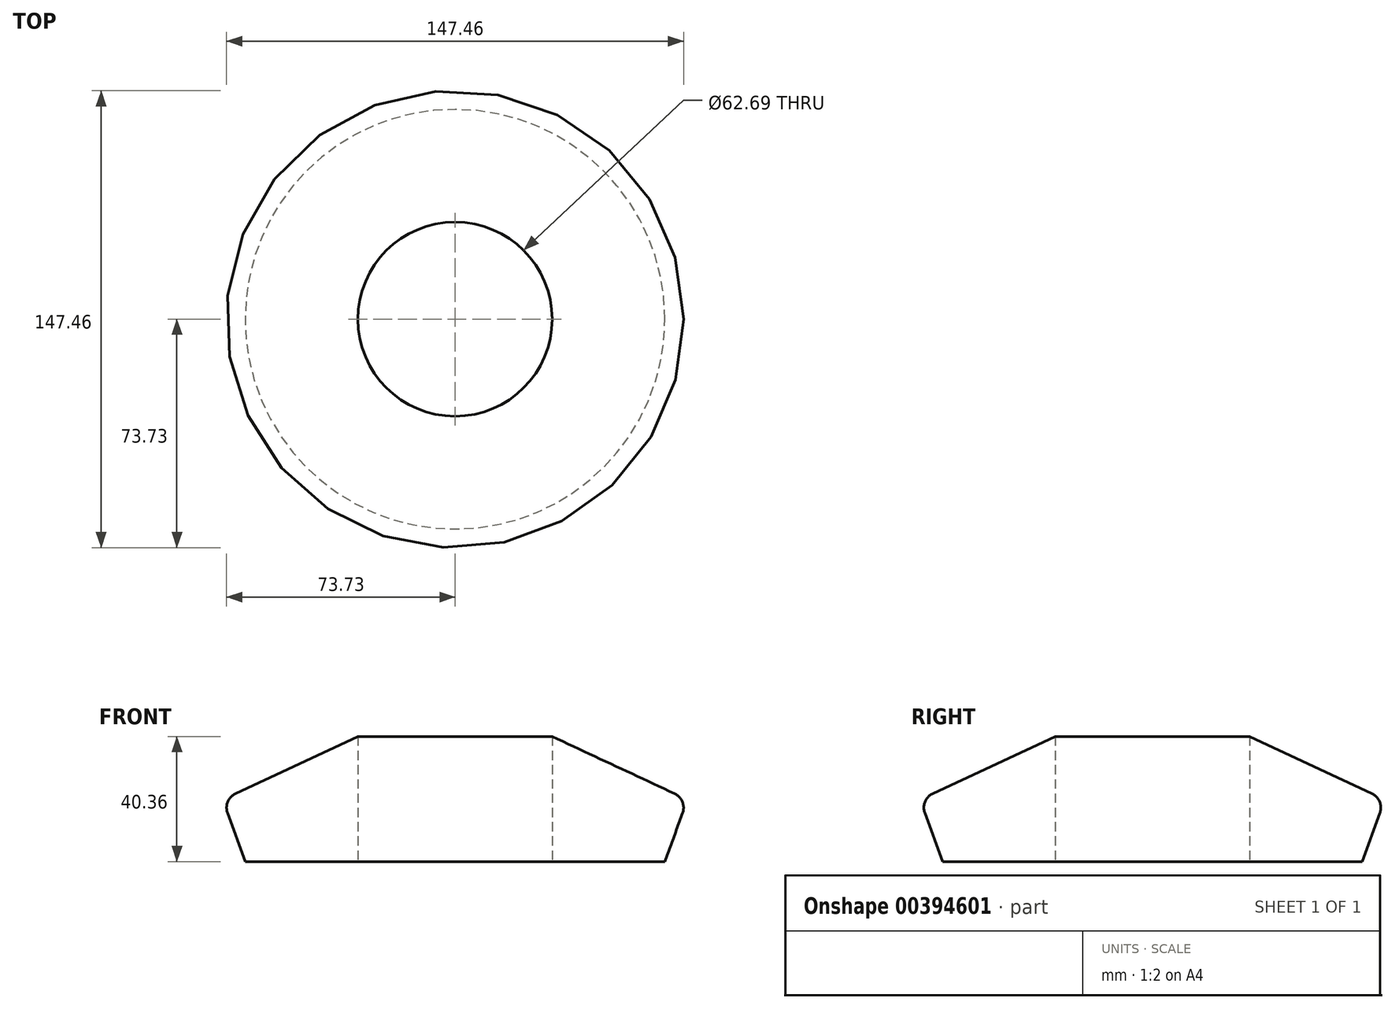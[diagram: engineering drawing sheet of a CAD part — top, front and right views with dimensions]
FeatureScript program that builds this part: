
annotation { "Feature Type Name" : "Feature", "Feature Type Description" : "" }
export const myFeature = defineFeature(function(context is Context, id is Id, definition is map)
    precondition{}
    {
        {
            var Q0;
            Q0=qCreatedBy(makeId("Top.planeOp"),FACE);
            var sketch = newSketch(context, id + "F0", { "sketchPlane" : qUnion([Q0])});
            skCircle(sketch, "E0", {"center": v(0, 0) * mm, "radius": 75 * mm});
            skSolve(sketch);
        }
        {
            var Q0;
            Q0 = qSketchRegion(id + "F0", true);
            extrude(context, id + "F1", {"entities" : qUnion([Q0]), "depth" : 50 * mm, "hasDraft" : true, "draftAngle" : 65 * degree, "draftPullDirection" : true, "hasSecondDirection" : true, "secondDirectionOppositeDirection" : true, "secondDirectionDepth" : 20 * mm, "hasSecondDirectionDraft" : true, "secondDirectionDraftAngle" : 20 * degree, "secondDirectionDraftPullDirection" : true});
        }
        {
            var Q0;
            {var subQ0=makeQuery(id+"F1.opExtrude","SWEPT_FACE",FACE,{"disambiguationData":[OSD([sQuery(id+"F0.wireOp",EDGE,"E0")])]});Q0=makeQuery(id+"F1.*.booleanUnion.opBoolean","MERGE",EDGE,{"derivedFrom":[makeQuery(id+"F1.*.split.splitOp","SPLIT_SURFACE_INTERSECT",EDGE,{"derivedFrom":[subQ0]}),makeQuery(id+"F1.*.split.splitOp","SPLIT_SURFACE_INTERSECT",EDGE,{"derivedFrom":[subQ0],"isFromBackBody":true})]});}
            fillet(context, id + "F2", {"entities" : qUnion([Q0]), "radius" : 5 * mm, "tangentPropagation" : true, "allowEdgeOverflow" : false});
        }
        {
            var Q0;
            Q0=qCreatedBy(makeId("Top.planeOp"),FACE);
            var sketch = newSketch(context, id + "F3", { "sketchPlane" : qUnion([Q0])});
            skCircle(sketch, "E1", {"center": v(0, 0) * mm, "radius": 31.34 * mm});
            skSolve(sketch);
        }
        {
            var Q0;
            Q0 = qSketchRegion(id + "F3", true);
            extrude(context, id + "F4", {"entities" : qUnion([Q0]), "operationType" : NewBodyOperationType.REMOVE, "depth" : 50 * mm, "hasSecondDirection" : true, "secondDirectionOppositeDirection" : true, "secondDirectionDepth" : 25 * mm});
        }
    });
